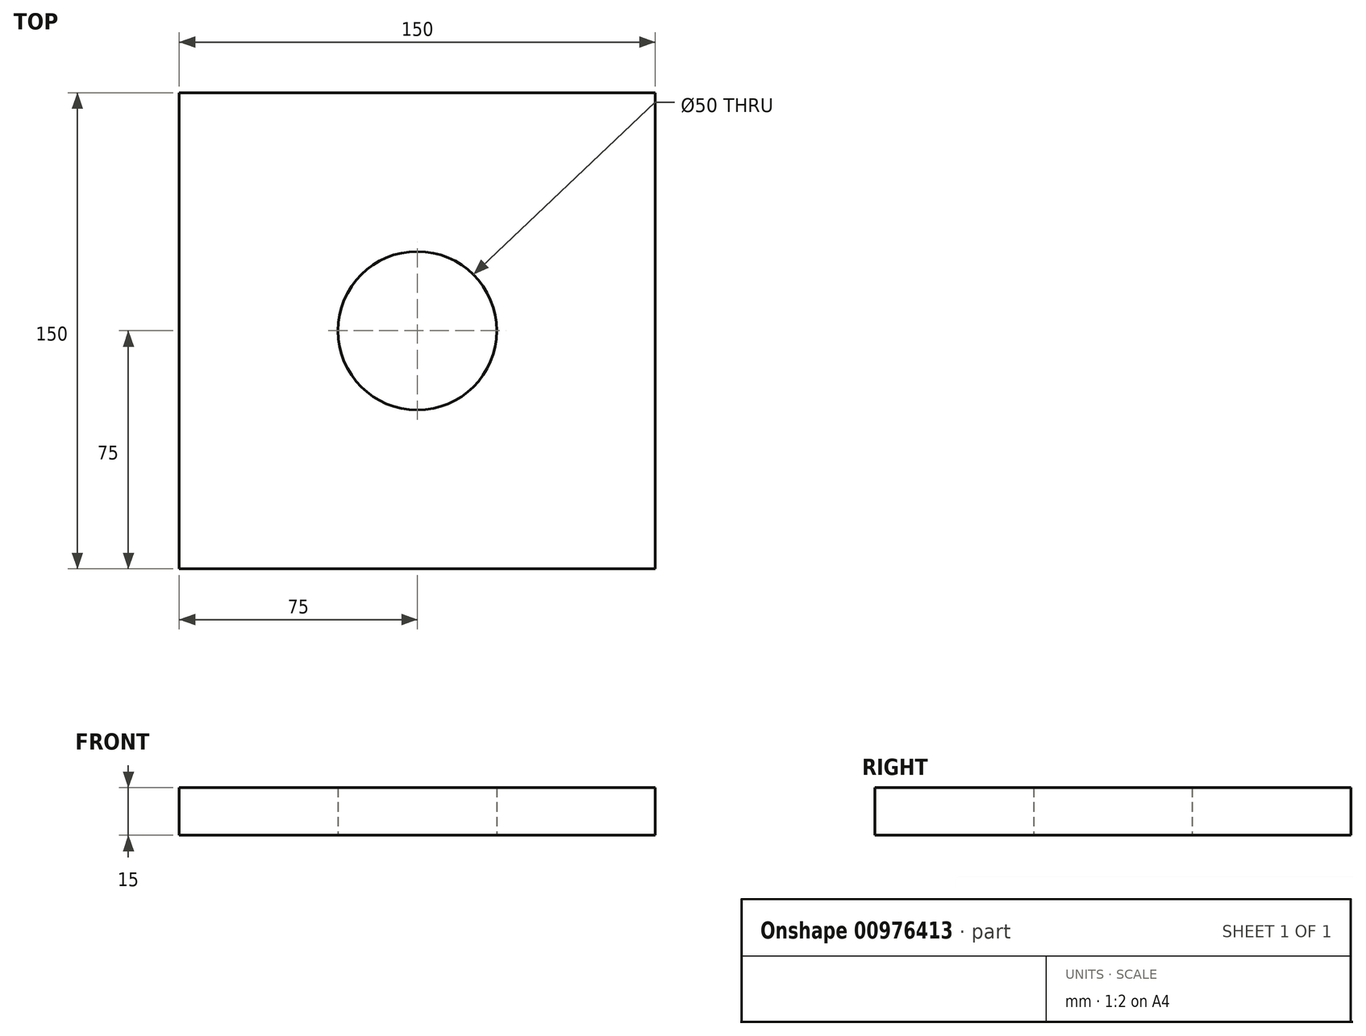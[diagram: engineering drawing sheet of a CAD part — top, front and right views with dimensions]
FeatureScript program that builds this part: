
annotation { "Feature Type Name" : "Feature", "Feature Type Description" : "" }
export const myFeature = defineFeature(function(context is Context, id is Id, definition is map)
    precondition{}
    {
        {
            var Q0;
            Q0=qCreatedBy(makeId("Top.planeOp"),FACE);
            var sketch = newSketch(context, id + "F0", { "sketchPlane" : qUnion([Q0])});
            skLineSegment(sketch, "E0.bottom", {"start": v(75, -75) * mm, "end": v(-75, -75) * mm});
            skLineSegment(sketch, "E0.top", {"start": v(75, 75) * mm, "end": v(-75, 75) * mm});
            skLineSegment(sketch, "E0.left", {"start": v(75, -75) * mm, "end": v(75, 75) * mm});
            skLineSegment(sketch, "E0.right", {"start": v(-75, -75) * mm, "end": v(-75, 75) * mm});
            skPoint(sketch, "E0.middle", {"position": v(0, 0) * mm});
            skCircle(sketch, "E1", {"center": v(0, 0) * mm, "radius": 25 * mm});
            skSolve(sketch);
        }
        {
            var Q0;
            Q0 = qSketchRegion(id + "F0", true);
            extrude(context, id + "F1", {"entities" : qUnion([Q0]), "depth" : 15 * mm, "offsetDistance" : 25 * mm});
        }
    });
